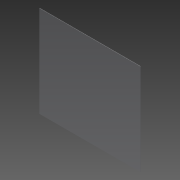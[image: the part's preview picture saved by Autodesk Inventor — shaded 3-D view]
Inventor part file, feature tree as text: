
AUTODESK INVENTOR PART (.ipt)
format: ipt  version: 2013 (Build 170138000, 138)  size: 64,512 bytes
history: native  units: in
note: dims shown in document units (in); Inventor stores cm internally (conversion verified against a paired STEP export)
features: extrude x1, sketch x1
ambient origin geometry x8: Origin, YZ Plane, XZ Plane, XY Plane, X Axis, Y Axis, Z Axis, Center Point
bodies: Solid1 (feature_tree)
feature tree (2):
  extrude  "Extrusion1"  Depth=48.0in
  sketch  "Sketch1"  dims[d0=53.0in d1=48.0in d2=0.25in d3=0.0in]
